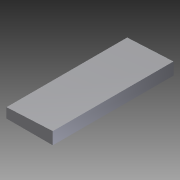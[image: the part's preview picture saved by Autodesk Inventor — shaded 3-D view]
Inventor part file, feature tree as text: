
AUTODESK INVENTOR PART (.ipt)
format: ipt  version: 2012 (Build 160160000, 160)  size: 69,120 bytes
history: native  units: in
note: dims shown in document units (in); Inventor stores cm internally (conversion verified against a paired STEP export)
features: extrude x1, sketch x1
ambient origin geometry x8: Origin, YZ Plane, XZ Plane, XY Plane, X Axis, Y Axis, Z Axis, Center Point
bodies: Solid1 (feature_tree)
feature tree (2):
  extrude  "Extrusion1"  Depth=8.25in
  sketch  "Sketch1"  dims[d2=38.75in d3=8.25in d4=10.25in d5=101.0in d6=0.0in]
